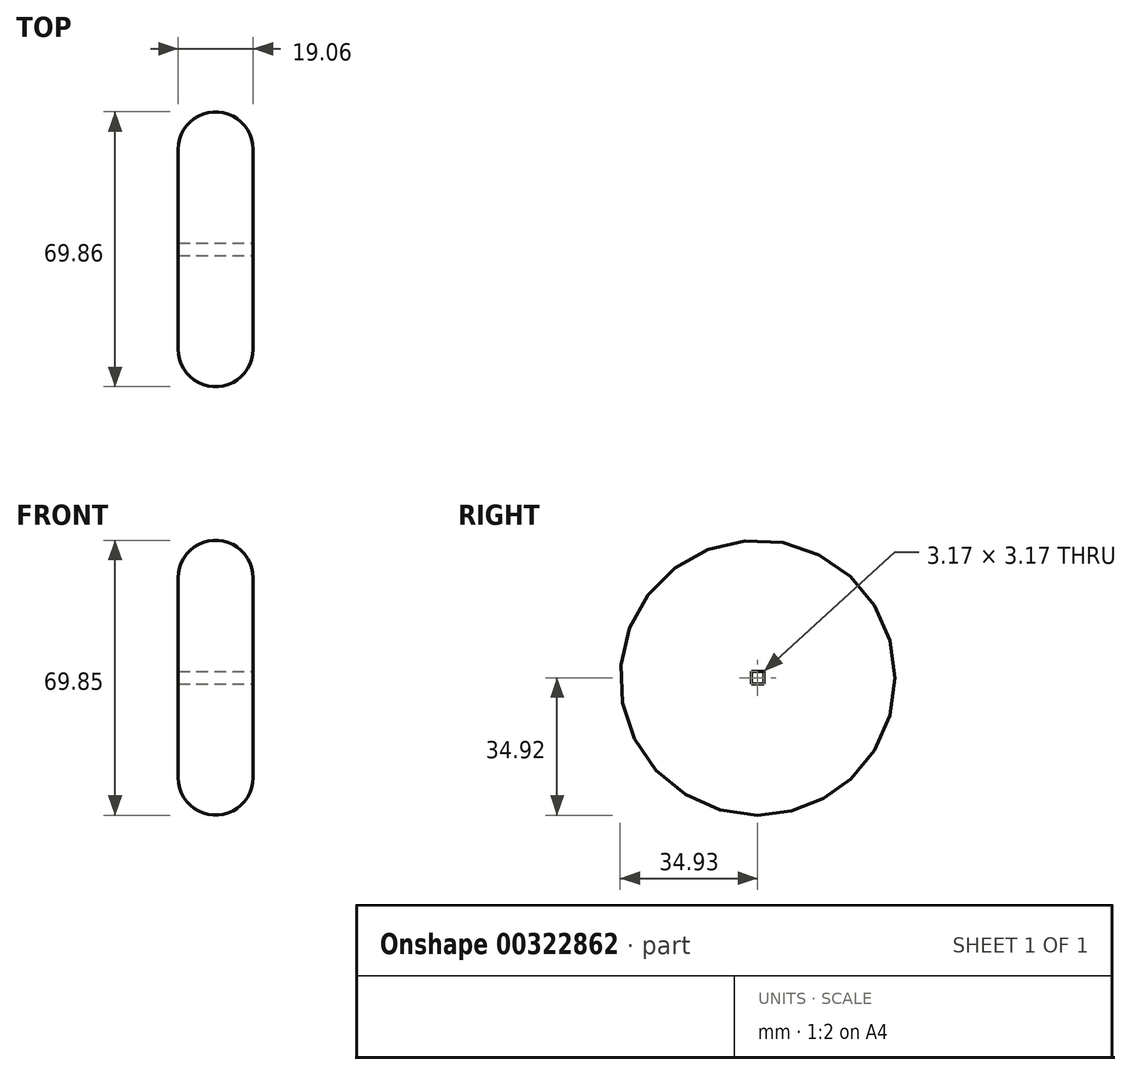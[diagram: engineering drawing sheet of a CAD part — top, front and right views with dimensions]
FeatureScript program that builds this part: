
annotation { "Feature Type Name" : "Feature", "Feature Type Description" : "" }
export const myFeature = defineFeature(function(context is Context, id is Id, definition is map)
    precondition{}
    {
        {
            var Q0;
            Q0=qCreatedBy(makeId("Top.planeOp"),FACE);
            var sketch = newSketch(context, id + "F0", { "sketchPlane" : qUnion([Q0])});
            skLineSegment(sketch, "E0.bottom", {"start": v(9.52, -34.93) * mm, "end": v(-9.53, -34.93) * mm});
            skLineSegment(sketch, "E0.top", {"start": v(0, 34.93) * mm, "end": v(0, 34.93) * mm});
            skLineSegment(sketch, "E0.left", {"start": v(9.52, -34.93) * mm, "end": v(9.53, 25.4) * mm});
            skLineSegment(sketch, "E0.right", {"start": v(-9.53, -34.93) * mm, "end": v(-9.52, 25.4) * mm});
            skPoint(sketch, "E0.middle", {"position": v(0, 0) * mm});
            skLineSegment(sketch, "E1", {"start": v(9.53, 0) * mm, "end": v(-9.53, 0) * mm});
            skPoint(sketch, "E2.visualSharp", {"position": v(9.53, 34.93) * mm});
            skArc(sketch, "E2.filletArc", {"start": v(9.52, 25.4) * mm, "mid": v(6.74, 32.14) * mm, "end": v(0, 34.93) * mm});
            skPoint(sketch, "E3.visualSharp", {"position": v(-9.52, 34.93) * mm});
            skArc(sketch, "E3.filletArc", {"start": v(0, 34.93) * mm, "mid": v(-6.74, 32.14) * mm, "end": v(-9.52, 25.4) * mm});
            skSolve(sketch);
        }
        {
            var Q0;
            {var subQ1=sQuery(id+"F0.wireOp",EDGE,"E1");Q0=makeQuery(id+"F0.imprint","IMPRINT",FACE,{"disambiguationData":[TD([[makeQuery(id+"F0.imprint","IMPRINT",EDGE,{"derivedFrom":subQ1}),-1.0]])]});}
            var Q1;
            Q1=sQuery(id+"F0.wireOp",EDGE,"E1");
            revolve(context, id + "F1", {"entities" : qUnion([Q0]), "axis" : qUnion([Q1]), "revolveType" : RevolveType.FULL});
        }
        {
            var Q0;
            Q0=makeQuery(id+"F1.opRevolve","SWEPT_FACE",FACE,{"disambiguationData":[OSD([sQuery(id+"F0.wireOp",EDGE,"E0.left")])]});
            var sketch = newSketch(context, id + "F2", { "sketchPlane" : qUnion([Q0])});
            skLineSegment(sketch, "E4.bottom", {"start": v(-1.59, -1.59) * mm, "end": v(1.59, -1.59) * mm});
            skLineSegment(sketch, "E4.top", {"start": v(-1.59, 1.59) * mm, "end": v(1.59, 1.59) * mm});
            skLineSegment(sketch, "E4.left", {"start": v(-1.59, -1.59) * mm, "end": v(-1.59, 1.59) * mm});
            skLineSegment(sketch, "E4.right", {"start": v(1.59, -1.59) * mm, "end": v(1.59, 1.59) * mm});
            skPoint(sketch, "E4.middle", {"position": v(0, 0) * mm});
            skSolve(sketch);
        }
        {
            var Q0;
            Q0=makeQuery(id+"F2.imprint","IMPRINT",FACE,{"disambiguationData":[TD([[makeQuery(id+"F2.imprint","IMPRINT",EDGE,{"derivedFrom":sQuery(id+"F2.wireOp",EDGE,"E4.bottom")}),1.0]])]});
            extrude(context, id + "F3", {"entities" : qUnion([Q0]), "operationType" : NewBodyOperationType.REMOVE, "oppositeDirection" : true, "depth" : 25 * mm});
        }
    });
